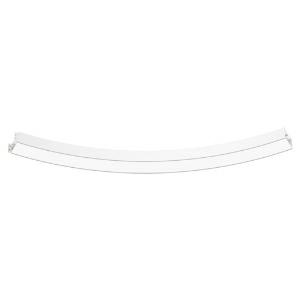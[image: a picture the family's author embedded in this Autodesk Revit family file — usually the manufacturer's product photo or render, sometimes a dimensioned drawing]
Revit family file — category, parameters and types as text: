
# Revit family: super-g_super-g__5400___51deg_hl_dir_indir__led__55_2w_8520lm_3000k_cri_80_430-1520_cef1
name_source: partatom
category: Leuchten
revit_build: Autodesk Revit 2016 (Build: 20190508_0715(x64)
units: mm (PartAtom-declared; Revit-internal decimal feet)

## family parameters
Basisbauteil = Fläche
Beim Laden mit Abzugskörper schneiden = Nein
Bemaßung runder Anschluss = Durchmesser verwenden
Gemeinsam genutzt = Nein
Lichtquelle = Nein
Raumberechnungspunkt = Nein
Teiletyp = Normal

## types (1)
- 430-1520- (1 x LED, 1065 lm, 3000K)
    Approval mark = CE
    Beschreibung = The insert consists of aluminum-extruded profile. Charming SOFT-EDGE design ensure unparalleled styling. The ballast is integrated and allows for an operation with 220-240V (50/60Hz). SUPER-G (# 430-1520) ist not dimmable (on/off).
    CIE Flux Codes = 44 75 94 72 76
    Color Rendering = 1B/80…89
    Color Temperature = 3000K
    Height = 120 mm
    Hersteller = Prolicht
    Lamp Light Flux = 1065 lm
    Lamp count = 1
    Lampe = 1 x LED
    Length = 300 mm
    Luminous efficacy = 107 lm/W
    ModVariant = Nein
    Modell = 430-1520
    Mounting Place = Ceiling
    Mounting Type = Pendant
    Number of Poles = 1
    OnlyDefault = Ja
    Power Factor = 1
    Product Name = SUPER-G__SUPER-G  5400 / 51° HL dir/indir. LED: 55,2W 8520lm 3000K CRI:80
    Product group = Suspended profile systems
    ProductGroupID = 944
    Protection Class = Protection class I
    Protection Degree = IP 20
    RLX_Detail_Level = 1
    RlxData = <blob elided: 34085 chars, md5=f16b7670>
    Scheinlast = 61 VA
    Socket = socket
    Standby Power = 0 W
    System Light Flux = 6475 lm
    System Power = 61 W
    Typenbild = 430-1520.jpg
    URL = http://relux.com
    VarID = 430-1520-
    Voltage = 0 V
    Vorgabe-Ansicht = 1800 mm
    Weight = 0.00 kg
    Width = 150 mm

## geometry (parser evidence)
native form markers: Sweep x56
no freeform markers — native parametric forms only
